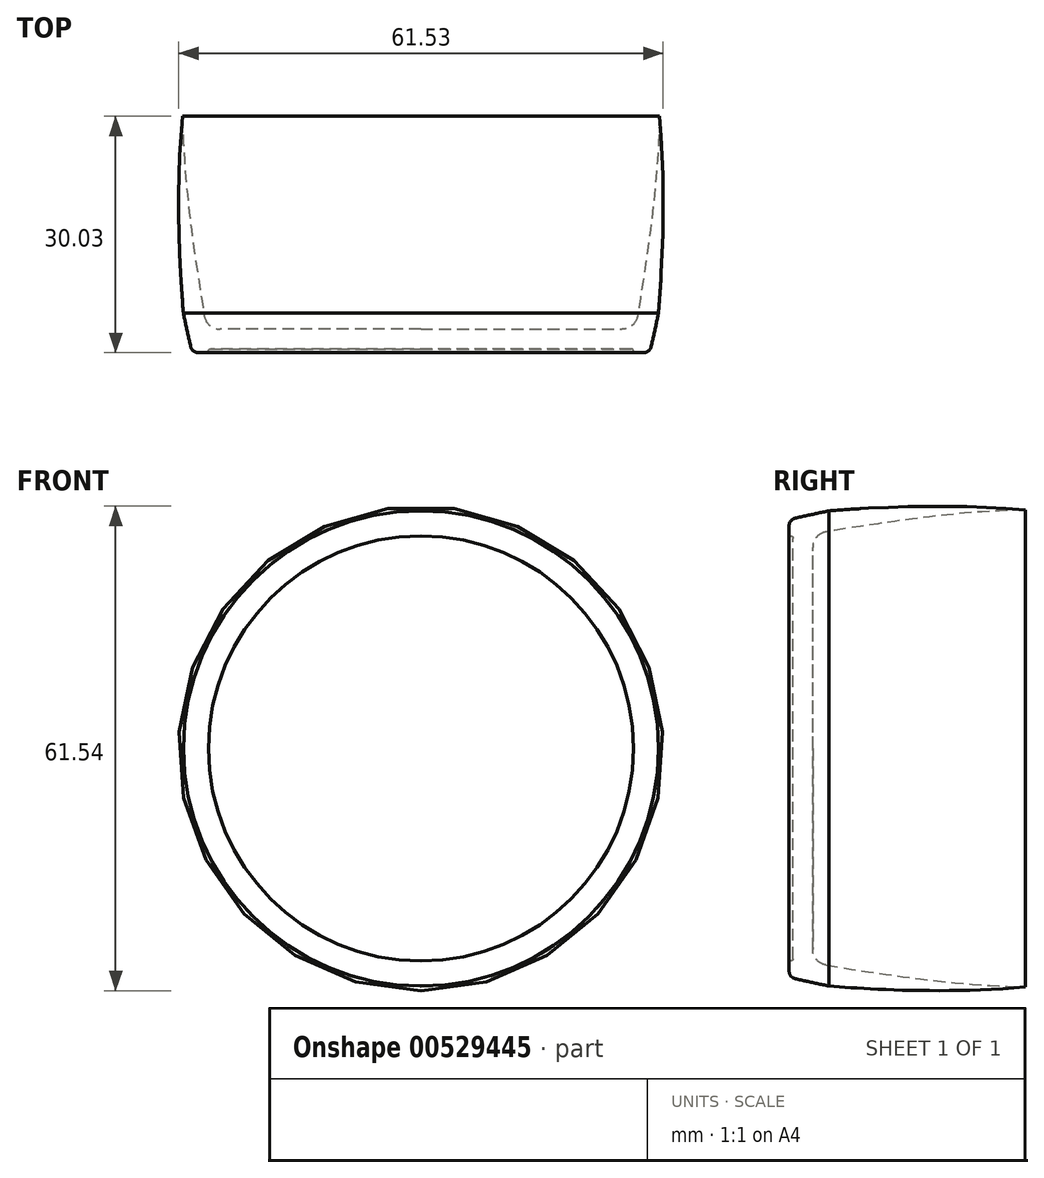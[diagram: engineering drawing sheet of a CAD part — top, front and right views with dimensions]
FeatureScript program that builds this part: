
annotation { "Feature Type Name" : "Feature", "Feature Type Description" : "" }
export const myFeature = defineFeature(function(context is Context, id is Id, definition is map)
    precondition{}
    {
        {
            var Q0;
            Q0=qCreatedBy(makeId("Top.planeOp"),FACE);
            var sketch = newSketch(context, id + "F0", { "sketchPlane" : qUnion([Q0])});
            skLineSegment(sketch, "E0", {"start": v(28.05, -26) * mm, "end": v(28.05, -25.5) * mm});
            skLineSegment(sketch, "E1", {"start": v(28.05, -25.5) * mm, "end": v(1.35, -25.5) * mm});
            skLineSegment(sketch, "E2", {"start": v(0.05, -25.8) * mm, "end": v(0.05, -25.8) * mm});
            skLineSegment(sketch, "E3", {"start": v(-0.15, -26) * mm, "end": v(-0.23, -26) * mm});
            skLineSegment(sketch, "E4", {"start": v(-6.08, 54) * mm, "end": v(-6.68, 54) * mm});
            skLineSegment(sketch, "E5", {"start": v(-2.03, -26) * mm, "end": v(-2.03, -26) * mm});
            skLineSegment(sketch, "E6", {"start": v(-4.98, -23) * mm, "end": v(-4.95, -23) * mm});
            skLineSegment(sketch, "E7", {"start": v(28.05, -25.5) * mm, "end": v(28.05, -23) * mm});
            skLineSegment(sketch, "E8", {"start": v(2.5, -23) * mm, "end": v(28.05, -23) * mm});
            skLineSegment(sketch, "E9", {"start": v(-6.68, 54) * mm, "end": v(-6.08, 54) * mm});
            skFitSpline(sketch, "E10", {"points": [v(-5.95, 54) * mm, v(0.05, 34.5) * mm, v(-2.25, 4.03) * mm, v(-2.46, -16.14) * mm, v(-1.95, -23) * mm], "startDerivative": vector(30.49, -68.52) * mm, "endDerivative": vector(3.43, -39.56) * mm});
            skPoint(sketch, "E11.visualSharp", {"position": v(-4.95, -26) * mm});
            skPoint(sketch, "E12.orphan", {"position": v(-3.05, -26) * mm});
            skPoint(sketch, "E13.start.orphan", {"position": v(-2.45, -26) * mm});
            skPoint(sketch, "E14.orphan", {"position": v(-4.95, 54) * mm});
            skPoint(sketch, "E15.end.orphan", {"position": v(2.05, 34.5) * mm});
            skPoint(sketch, "E16.visualSharp", {"position": v(-6.95, 54) * mm});
            skArc(sketch, "E16.filletArc", {"start": v(-6.68, 54) * mm, "mid": v(-6.84, 53.92) * mm, "end": v(-6.87, 53.74) * mm});
            skArc(sketch, "E17.filletArc", {"start": v(-5.9, 53.88) * mm, "mid": v(-5.97, 53.97) * mm, "end": v(-6.08, 54) * mm});
            skPoint(sketch, "E18.visualSharp", {"position": v(0.05, -26) * mm});
            skPoint(sketch, "E19.visualSharp", {"position": v(0.05, -25.5) * mm});
            skPoint(sketch, "E20.visualSharp", {"position": v(-2.03, -26) * mm});
            skLineSegment(sketch, "E21", {"start": v(0.05, -26) * mm, "end": v(0.85, -26) * mm});
            skLineSegment(sketch, "E22", {"start": v(0.05, -26) * mm, "end": v(-0.15, -26) * mm});
            skLineSegment(sketch, "E23", {"start": v(1.05, -25.8) * mm, "end": v(1.05, -25.8) * mm});
            skFitSpline(sketch, "E24", {"points": [v(-1.03, -26) * mm, v(-2.95, -16.14) * mm, v(-3.95, 4.03) * mm, v(-2.95, 34.5) * mm, v(-6.87, 53.74) * mm], "startDerivative": vector(-11.55, 50.68) * mm, "endDerivative": vector(-20.5, 70.68) * mm});
            skFitSpline(sketch, "E25", {"points": [v(0.8, -23) * mm, v(-2.25, 4.03) * mm, v(0.05, 34.5) * mm], "startDerivative": vector(-8.92, 54.82) * mm, "endDerivative": vector(7.24, 60.13) * mm});
            skArc(sketch, "E26.filletArc", {"start": v(1.35, -25.5) * mm, "mid": v(1.13, -25.59) * mm, "end": v(1.05, -25.8) * mm});
            skPoint(sketch, "E27.visualSharp", {"position": v(1.05, -26) * mm});
            skArc(sketch, "E27.filletArc", {"start": v(0.85, -26) * mm, "mid": v(0.99, -25.94) * mm, "end": v(1.05, -25.8) * mm});
            skArc(sketch, "E28.filletArc", {"start": v(-1.2, -25.22) * mm, "mid": v(-0.85, -25.78) * mm, "end": v(-0.23, -26) * mm});
            skArc(sketch, "E29.filletArc", {"start": v(0.53, -21.32) * mm, "mid": v(1.2, -22.52) * mm, "end": v(2.5, -23) * mm});
            skSolve(sketch);
        }
        {
            var Q0;
            Q0=makeQuery(id+"F0.imprint","IMPRINT",FACE,{"disambiguationData":[TD([[makeQuery(id+"F0.imprint","IMPRINT",EDGE,{"derivedFrom":sQuery(id+"F0.wireOp",EDGE,"E1")}),-1.0]])]});
            var Q1;
            Q1=sQuery(id+"F0.wireOp",EDGE,"E0");
            revolve(context, id + "F1", {"entities" : qUnion([Q0]), "axis" : qUnion([Q1]), "revolveType" : RevolveType.FULL});
        }
    });
